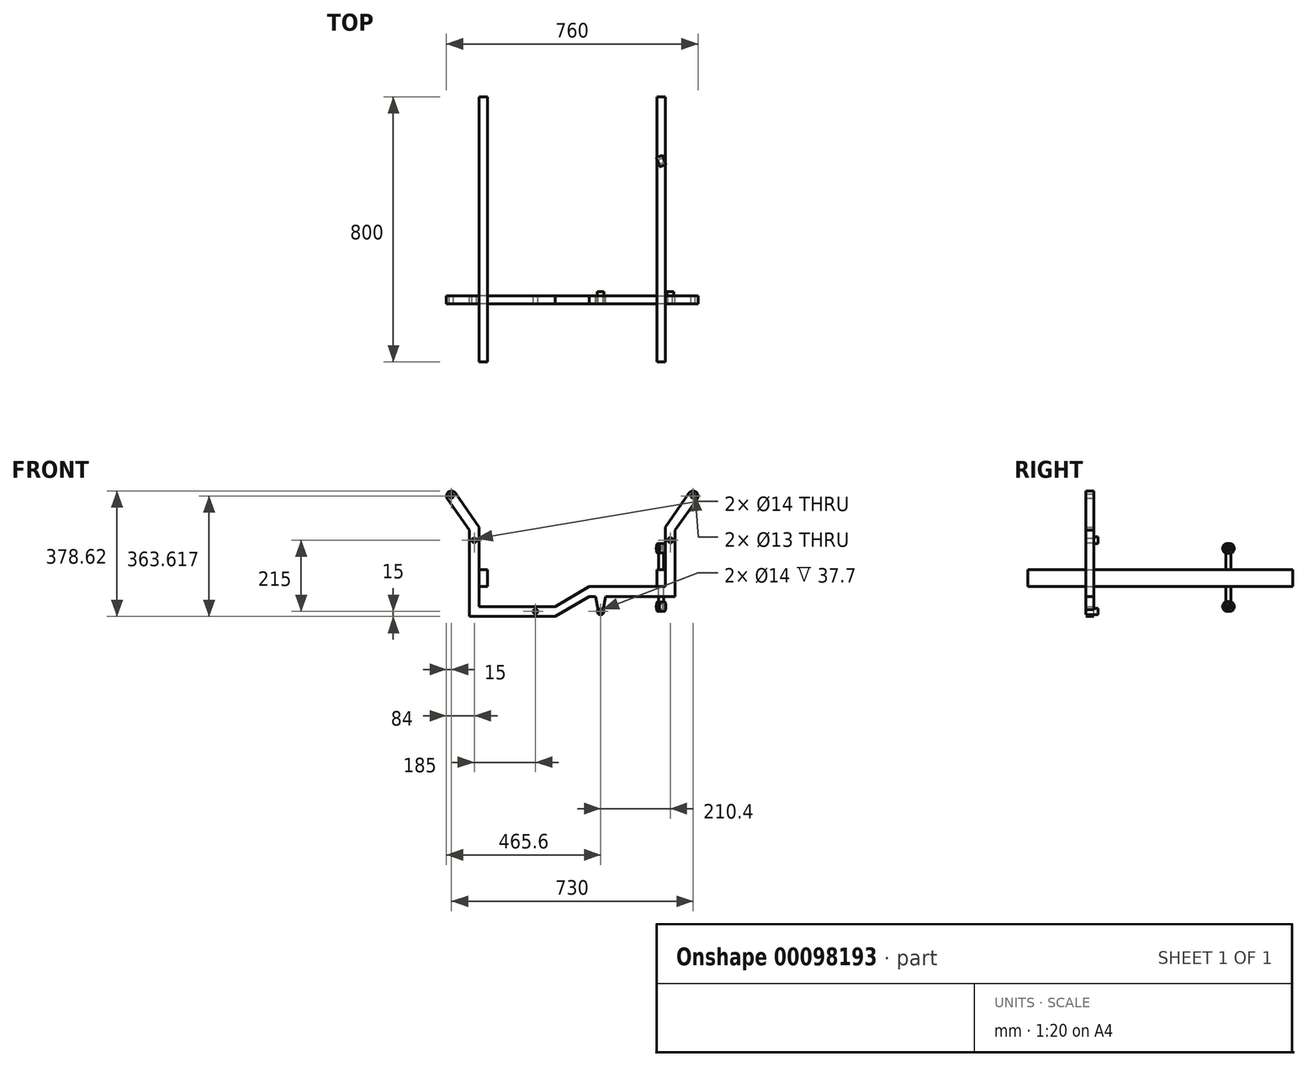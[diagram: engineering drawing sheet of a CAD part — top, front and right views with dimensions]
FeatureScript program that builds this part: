
annotation { "Feature Type Name" : "Feature", "Feature Type Description" : "" }
export const myFeature = defineFeature(function(context is Context, id is Id, definition is map)
    precondition{}
    {
        {
            var Q0;
            Q0=qCreatedBy(makeId("Front.planeOp"),FACE);
            var sketch = newSketch(context, id + "F0", { "sketchPlane" : qUnion([Q0])});
            skLineSegment(sketch, "E0", {"start": v(-301.72, 102.23) * mm, "end": v(-230, 0) * mm});
            skLineSegment(sketch, "E1", {"start": v(332, -180) * mm, "end": v(332, 0) * mm});
            skLineSegment(sketch, "E2", {"start": v(332, 0) * mm, "end": v(403.72, 102.23) * mm});
            skLineSegment(sketch, "E3", {"start": v(-326.28, 85) * mm, "end": v(-260, -9.47) * mm});
            skLineSegment(sketch, "E4", {"start": v(-260, -9.47) * mm, "end": v(-260, -270) * mm});
            skLineSegment(sketch, "E5", {"start": v(-260, -270) * mm, "end": v(0, -270) * mm});
            skLineSegment(sketch, "E6", {"start": v(102, -210) * mm, "end": v(0, -270) * mm});
            skLineSegment(sketch, "E7", {"start": v(362, -210) * mm, "end": v(362, -9.47) * mm});
            skLineSegment(sketch, "E8", {"start": v(362, -9.47) * mm, "end": v(428.28, 85) * mm});
            skLineSegment(sketch, "E9", {"start": v(0, -240) * mm, "end": v(102, -180) * mm});
            skLineSegment(sketch, "E10", {"start": v(0, -240) * mm, "end": v(-230, -240) * mm});
            skLineSegment(sketch, "E11", {"start": v(-230, 0) * mm, "end": v(-230, -240) * mm});
            skLineSegment(sketch, "E12", {"start": v(102, -180) * mm, "end": v(332, -180) * mm});
            skCircle(sketch, "E13", {"center": v(-245, -40) * mm, "radius": 7 * mm});
            skCircle(sketch, "E14", {"center": v(347, -40) * mm, "radius": 7 * mm});
            skArc(sketch, "E15", {"start": v(-301.72, 102.23) * mm, "mid": v(-322.61, 105.9) * mm, "end": v(-326.28, 85) * mm});
            skArc(sketch, "E16", {"start": v(428.28, 85) * mm, "mid": v(424.61, 105.9) * mm, "end": v(403.72, 102.23) * mm});
            skCircle(sketch, "E17", {"center": v(-314, 93.62) * mm, "radius": 6.5 * mm});
            skCircle(sketch, "E18", {"center": v(416, 93.62) * mm, "radius": 6.5 * mm});
            skLineSegment(sketch, "E19.bottom", {"start": v(332, -180) * mm, "end": v(306.6, -180) * mm});
            skLineSegment(sketch, "E19.top", {"start": v(332, -129.2) * mm, "end": v(306.6, -129.2) * mm, "construction": true});
            skLineSegment(sketch, "E19.left", {"start": v(332, -180) * mm, "end": v(332, -129.2) * mm});
            skLineSegment(sketch, "E19.right", {"start": v(306.6, -180) * mm, "end": v(306.6, -129.2) * mm, "construction": true});
            skCircle(sketch, "E20", {"center": v(-60, -255) * mm, "radius": 7 * mm});
            skPoint(sketch, "E21", {"position": v(-230, -255) * mm});
            skLineSegment(sketch, "E22", {"start": v(-230, -240) * mm, "end": v(-230, -270) * mm, "construction": true});
            skCircle(sketch, "E23", {"center": v(136.6, -255) * mm, "radius": 7 * mm});
            skLineSegment(sketch, "E24", {"start": v(102, -210) * mm, "end": v(121.6, -210) * mm});
            skLineSegment(sketch, "E25", {"start": v(151.6, -210) * mm, "end": v(362, -210) * mm});
            skArc(sketch, "E26", {"start": v(144.6, -249) * mm, "mid": v(136.6, -265) * mm, "end": v(128.6, -249) * mm});
            skLineSegment(sketch, "E27", {"start": v(121.6, -210) * mm, "end": v(128.6, -249) * mm});
            skLineSegment(sketch, "E28", {"start": v(151.6, -210) * mm, "end": v(144.6, -249) * mm});
            skSolve(sketch);
        }
        {
            var Q0;
            Q0=makeQuery(id+"F0.imprint","IMPRINT",FACE,{"disambiguationData":[TD([[makeQuery(id+"F0.imprint","IMPRINT",EDGE,{"derivedFrom":sQuery(id+"F0.wireOp",EDGE,"E0")}),-1.0]])]});
            extrude(context, id + "F1", {"entities" : qUnion([Q0]), "depth" : 25 * mm});
        }
        {
            var Q0;
            Q0=qCreatedBy(makeId("Front.planeOp"),FACE);
            var sketch = newSketch(context, id + "F2", { "sketchPlane" : qUnion([Q0])});
            skLineSegment(sketch, "E29.bottom", {"start": v(306.6, -129.2) * mm, "end": v(332, -129.2) * mm});
            skLineSegment(sketch, "E29.top", {"start": v(306.6, -180) * mm, "end": v(332, -180) * mm});
            skLineSegment(sketch, "E29.left", {"start": v(306.6, -129.2) * mm, "end": v(306.6, -180) * mm});
            skLineSegment(sketch, "E29.right", {"start": v(332, -129.2) * mm, "end": v(332, -180) * mm});
            skLineSegment(sketch, "E30.bottom", {"start": v(-230, -129.2) * mm, "end": v(-204.6, -129.2) * mm});
            skLineSegment(sketch, "E30.top", {"start": v(-230, -180) * mm, "end": v(-204.6, -180) * mm});
            skLineSegment(sketch, "E30.left", {"start": v(-230, -129.2) * mm, "end": v(-230, -180) * mm});
            skLineSegment(sketch, "E30.right", {"start": v(-204.6, -129.2) * mm, "end": v(-204.6, -180) * mm});
            skSolve(sketch);
        }
        {
            var Q0;
            Q0=qSketchRegion(id+"F2",true);
            extrude(context, id + "F3", {"entities" : qUnion([Q0]), "operationType" : NewBodyOperationType.ADD, "depth" : 200 * mm, "hasSecondDirection" : true, "secondDirectionOppositeDirection" : true, "secondDirectionDepth" : 600 * mm});
        }
        {
            var Q0;
            Q0=qCreatedBy(makeId("Right.planeOp"),FACE);
            var sketch = newSketch(context, id + "F4", { "sketchPlane" : qUnion([Q0])});
            skLineSegment(sketch, "E31", {"start": v(0, -64.6) * mm, "end": v(406.4, -64.6) * mm, "construction": true});
            skSolve(sketch);
        }
        {
            var Q0;
            Q0=makeQuery(id+"F3.opExtrude","SWEPT_FACE",FACE,{"disambiguationData":[OSD([sQuery(id+"F2.wireOp",EDGE,"E29.bottom")])]});
            var sketch = newSketch(context, id + "F5", { "sketchPlane" : qUnion([Q0])});
            skCircle(sketch, "E32", {"center": v(319.3, 406.4) * mm, "radius": 7.5 * mm});
            skPoint(sketch, "E33", {"position": v(319.3, 600) * mm});
            skLineSegment(sketch, "E34", {"start": v(319.3, 600) * mm, "end": v(319.3, 406.4) * mm, "construction": true});
            skLineSegment(sketch, "E35", {"start": v(319.3, 406.4) * mm, "end": v(250.9, 594.34) * mm});
            skSolve(sketch);
        }
        {
            var Q0;
            Q0=qSketchRegion(id+"F5",true);
            extrude(context, id + "F6", {"entities" : qUnion([Q0]), "operationType" : NewBodyOperationType.ADD, "depth" : 65 * mm});
        }
        {
            var Q0;
            Q0=qCreatedBy(makeId("Right.planeOp"),FACE);
            var Q1;
            Q1=sQuery(id+"F5.wireOp",EDGE,"E35");
            cPlane(context, id + "F7", {"entities" : qUnion([Q0, Q1]), "cplaneType" : CPlaneType.LINE_ANGLE, "offset" : 150 * mm, "angle" : 0 * degree, "width" : 150 * mm, "height" : 150 * mm});
        }
        {
            var Q0;
            Q0=qCreatedBy(id+"F7.planeOp",FACE);
            var sketch = newSketch(context, id + "F8", { "sketchPlane" : qUnion([Q0])});
            skCircle(sketch, "E36", {"center": v(-272.68, -64.6) * mm, "radius": 15 * mm});
            skCircle(sketch, "E37", {"center": v(-272.68, -64.6) * mm, "radius": 7 * mm});
            skSolve(sketch);
        }
        {
            var Q0;
            Q0=qSketchRegion(id+"F8",true);
            extrude(context, id + "F9", {"entities" : qUnion([Q0]), "operationType" : NewBodyOperationType.ADD, "endBound" : BoundingType.SYMMETRIC, "depth" : 20 * mm});
        }
        {
            var Q0;
            Q0=qCreatedBy(id+"F7.planeOp",FACE);
            var sketch = newSketch(context, id + "F10", { "sketchPlane" : qUnion([Q0])});
            skCircle(sketch, "E38", {"center": v(-272.68, -240) * mm, "radius": 15 * mm});
            skCircle(sketch, "E39", {"center": v(-272.68, -240) * mm, "radius": 7 * mm});
            skSolve(sketch);
        }
        {
            var Q0;
            Q0=qSketchRegion(id+"F10",true);
            extrude(context, id + "F11", {"entities" : qUnion([Q0]), "endBound" : BoundingType.SYMMETRIC, "depth" : 20 * mm});
        }
        {
            var Q0;
            {var subQ0=sQuery(id+"F2.wireOp",EDGE,"E29.left");var subQ1=sQuery(id+"F2.wireOp",EDGE,"E29.right");var subQ2=sQuery(id+"F2.wireOp",EDGE,"E29.top");Q0=makeQuery(id+"F3.boolean.opBoolean","SPLIT",FACE,{"disambiguationData":[TD([makeQuery(id+"F3.opExtrude","CAP_FACE",FACE,{"disambiguationData":[OSD([sQuery(id+"F2.wireOp",EDGE,"E29.bottom"),subQ2,subQ0,subQ1])],"isStart":true})])],"derivedFrom":makeQuery(id+"F3.opExtrude","SWEPT_FACE",FACE,{"disambiguationData":[OSD([subQ2])]})});}
            var sketch = newSketch(context, id + "F12", { "sketchPlane" : qUnion([Q0])});
            skCircle(sketch, "E40", {"center": v(319.3, -406.4) * mm, "radius": 7.5 * mm});
            skSolve(sketch);
        }
        {
            var Q0;
            Q0=qSketchRegion(id+"F12",true);
            var Q1;
            Q1=makeQuery(id+"F11.opExtrude","SWEPT_FACE",FACE,{"disambiguationData":[OSD([sQuery(id+"F10.wireOp",EDGE,"E38")])]});
            extrude(context, id + "F13", {"entities" : qUnion([Q0]), "operationType" : NewBodyOperationType.ADD, "endBound" : BoundingType.UP_TO_SURFACE, "endBoundEntityFace" : qUnion([Q1]), "depth" : 25 * mm});
        }
        {
            var Q0;
            Q0=makeQuery(id+"F0.imprint","IMPRINT",FACE,{"disambiguationData":[TD([[makeQuery(id+"F0.imprint","IMPRINT",EDGE,{"derivedFrom":sQuery(id+"F0.wireOp",EDGE,"E0")}),-1.0]])]});
            var sketch = newSketch(context, id + "F14", { "sketchPlane" : qUnion([Q0])});
            skCircle(sketch, "E41", {"center": v(136.6, -255) * mm, "radius": 10 * mm});
            skCircle(sketch, "E42", {"center": v(136.6, -255) * mm, "radius": 7 * mm});
            skSolve(sketch);
        }
        {
            var Q0;
            Q0=qSketchRegion(id+"F14",true);
            extrude(context, id + "F15", {"entities" : qUnion([Q0]), "operationType" : NewBodyOperationType.ADD, "oppositeDirection" : true, "depth" : 12.7 * mm});
        }
        {
            var Q0;
            Q0=makeQuery(id+"F0.imprint","IMPRINT",FACE,{"disambiguationData":[TD([[makeQuery(id+"F0.imprint","IMPRINT",EDGE,{"derivedFrom":sQuery(id+"F0.wireOp",EDGE,"E0")}),-1.0]])]});
            var sketch = newSketch(context, id + "F16", { "sketchPlane" : qUnion([Q0])});
            skCircle(sketch, "E43", {"center": v(347, -40) * mm, "radius": 10 * mm});
            skCircle(sketch, "E44", {"center": v(347, -40) * mm, "radius": 7 * mm});
            skSolve(sketch);
        }
        {
            var Q0;
            Q0=qSketchRegion(id+"F16",true);
            extrude(context, id + "F17", {"entities" : qUnion([Q0]), "operationType" : NewBodyOperationType.ADD, "oppositeDirection" : true, "depth" : 12.7 * mm});
        }
    });
